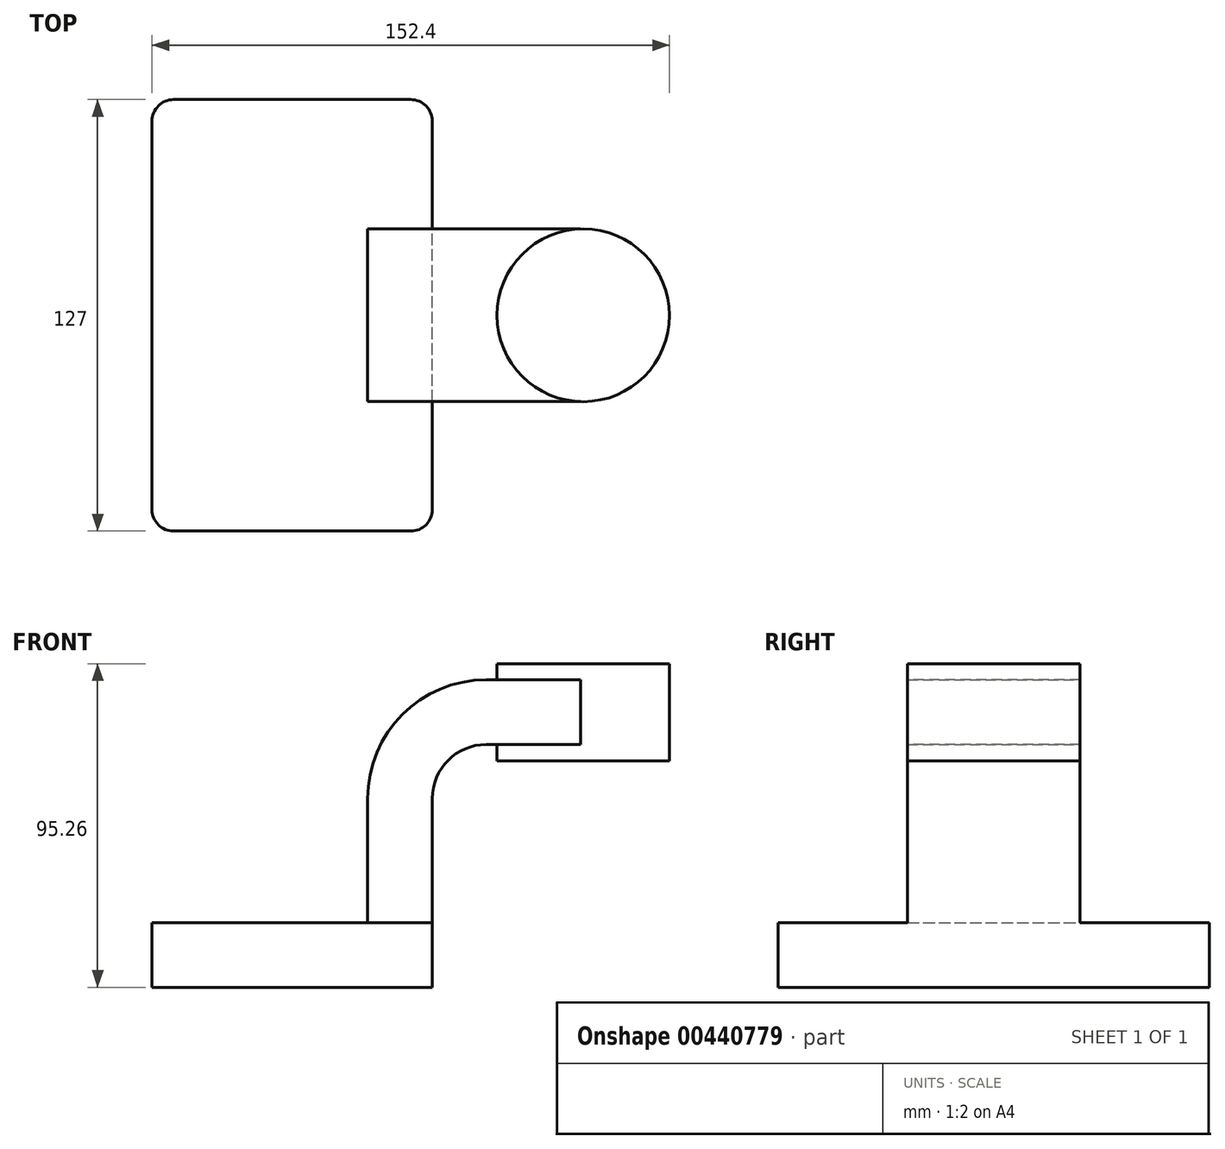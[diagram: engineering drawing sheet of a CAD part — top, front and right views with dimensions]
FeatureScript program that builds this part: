
annotation { "Feature Type Name" : "Feature", "Feature Type Description" : "" }
export const myFeature = defineFeature(function(context is Context, id is Id, definition is map)
    precondition{}
    {
        {
            var Q0;
            Q0=qCreatedBy(makeId("Front.planeOp"),FACE);
            var sketch = newSketch(context, id + "F0", { "sketchPlane" : qUnion([Q0])});
            skLineSegment(sketch, "E0.bottom", {"start": v(41.27, 9.53) * mm, "end": v(-41.28, 9.53) * mm});
            skLineSegment(sketch, "E0.top", {"start": v(41.28, -9.52) * mm, "end": v(-41.27, -9.52) * mm});
            skLineSegment(sketch, "E0.left", {"start": v(41.28, 9.53) * mm, "end": v(41.28, -9.52) * mm});
            skLineSegment(sketch, "E0.right", {"start": v(-41.28, 9.53) * mm, "end": v(-41.27, -9.52) * mm});
            skPoint(sketch, "E0.middle", {"position": v(0, 0) * mm});
            skLineSegment(sketch, "E1.bottom", {"start": v(111.12, 57.15) * mm, "end": v(60.33, 57.15) * mm});
            skLineSegment(sketch, "E1.top", {"start": v(111.12, 85.73) * mm, "end": v(60.32, 85.73) * mm});
            skLineSegment(sketch, "E1.left", {"start": v(111.12, 57.15) * mm, "end": v(111.12, 85.73) * mm});
            skLineSegment(sketch, "E1.right", {"start": v(60.33, 57.15) * mm, "end": v(60.32, 85.73) * mm});
            skPoint(sketch, "E1.middle", {"position": v(85.73, 71.44) * mm});
            skLineSegment(sketch, "E2", {"start": v(41.27, 9.53) * mm, "end": v(41.27, 46.05) * mm});
            skArc(sketch, "E3", {"start": v(41.27, 46.05) * mm, "mid": v(45.92, 57.28) * mm, "end": v(57.15, 61.93) * mm});
            skLineSegment(sketch, "E4", {"start": v(57.15, 61.93) * mm, "end": v(85.71, 61.93) * mm});
            skLineSegment(sketch, "E5.0", {"start": v(57.15, 80.98) * mm, "end": v(85.71, 80.98) * mm});
            skArc(sketch, "E5.1", {"start": v(22.23, 46.05) * mm, "mid": v(32.45, 70.75) * mm, "end": v(57.15, 80.98) * mm});
            skLineSegment(sketch, "E5.2", {"start": v(22.22, 9.53) * mm, "end": v(22.22, 46.05) * mm});
            skLineSegment(sketch, "E6", {"start": v(85.71, 80.98) * mm, "end": v(85.71, 61.93) * mm});
            skFitSpline(sketch, "E7", {"points": [v(-41.28, 9.53) * mm, v(57.15, 80.98) * mm], "startDerivative": vector(-0.53, 78.82) * mm, "endDerivative": vector(128.59, -0.24) * mm});
            skLineSegment(sketch, "E8", {"start": v(85.71, 85.73) * mm, "end": v(85.71, 57.15) * mm});
            skSolve(sketch);
        }
        {
            var Q0;
            Q0=makeQuery(id+"F0.imprint","IMPRINT",FACE,{"disambiguationData":[TD([[makeQuery(id+"F0.imprint","IMPRINT",EDGE,{"derivedFrom":sQuery(id+"F0.wireOp",EDGE,"E0.top")}),-1.0]])]});
            extrude(context, id + "F1", {"entities" : qUnion([Q0]), "endBound" : BoundingType.SYMMETRIC, "depth" : 127 * mm});
        }
        {
            var Q0;
            {var subQ0=sQuery(id+"F0.wireOp",EDGE,"E4");var subQ1=sQuery(id+"F0.wireOp",EDGE,"E1.right");var subQ2=makeQuery(id+"F0.imprint","INTERSECT",VERTEX,{"derivedFrom":[subQ1,subQ0]});Q0=makeQuery(id+"F0.imprint","IMPRINT",FACE,{"disambiguationData":[TD([[makeQuery(id+"F0.imprint","IMPRINT",EDGE,{"disambiguationData":[TD([[subQ2,-1.0]])],"derivedFrom":subQ1}),-1.0]])]});}
            var Q1;
            {var subQ1=sQuery(id+"F0.wireOp",EDGE,"E2");Q1=makeQuery(id+"F0.imprint","IMPRINT",FACE,{"disambiguationData":[TD([[makeQuery(id+"F0.imprint","IMPRINT",EDGE,{"derivedFrom":subQ1}),1.0]])]});}
            extrude(context, id + "F2", {"entities" : qUnion([Q0, Q1]), "operationType" : NewBodyOperationType.ADD, "endBound" : BoundingType.SYMMETRIC, "depth" : 50.8 * mm});
        }
        {
            var Q0;
            Q0=makeQuery(id+"F0.imprint","IMPRINT",FACE,{"disambiguationData":[TD([[makeQuery(id+"F0.imprint","IMPRINT",EDGE,{"derivedFrom":sQuery(id+"F0.wireOp",EDGE,"E5.1")}),1.0]])]});
            extrude(context, id + "F3", {"entities" : qUnion([Q0]), "operationType" : NewBodyOperationType.ADD, "endBound" : BoundingType.SYMMETRIC, "depth" : 15.88 * mm});
        }
        {
            var Q0;
            {var subQ0=sQuery(id+"F0.wireOp",EDGE,"E1.left");Q0=makeQuery(id+"F0.imprint","IMPRINT",FACE,{"disambiguationData":[TD([[makeQuery(id+"F0.imprint","IMPRINT",EDGE,{"derivedFrom":subQ0}),1.0]])]});}
            var Q1;
            Q1=sQuery(id+"F0.wireOp",EDGE,"E8");
            revolve(context, id + "F4", {"operationType" : NewBodyOperationType.ADD, "entities" : qUnion([Q0]), "axis" : qUnion([Q1]), "revolveType" : RevolveType.FULL});
        }
        {
            var Q0;
            Q0=makeQuery(id+"F1.opExtrude","CAP_EDGE",EDGE,{"disambiguationData":[OSD([sQuery(id+"F0.wireOp",EDGE,"E0.left")])],"isStart":false});
            var Q1;
            Q1=makeQuery(id+"F1.opExtrude","CAP_EDGE",EDGE,{"disambiguationData":[OSD([sQuery(id+"F0.wireOp",EDGE,"E0.right")])],"isStart":false});
            var Q2;
            Q2=makeQuery(id+"F1.opExtrude","CAP_EDGE",EDGE,{"disambiguationData":[OSD([sQuery(id+"F0.wireOp",EDGE,"E0.right")])],"isStart":true});
            var Q3;
            Q3=makeQuery(id+"F1.opExtrude","CAP_EDGE",EDGE,{"disambiguationData":[OSD([sQuery(id+"F0.wireOp",EDGE,"E0.left")])],"isStart":true});
            fillet(context, id + "F5", {"entities" : qUnion([Q0, Q1, Q2, Q3]), "radius" : 6.35 * mm, "tangentPropagation" : true, "allowEdgeOverflow" : false});
        }
    });
